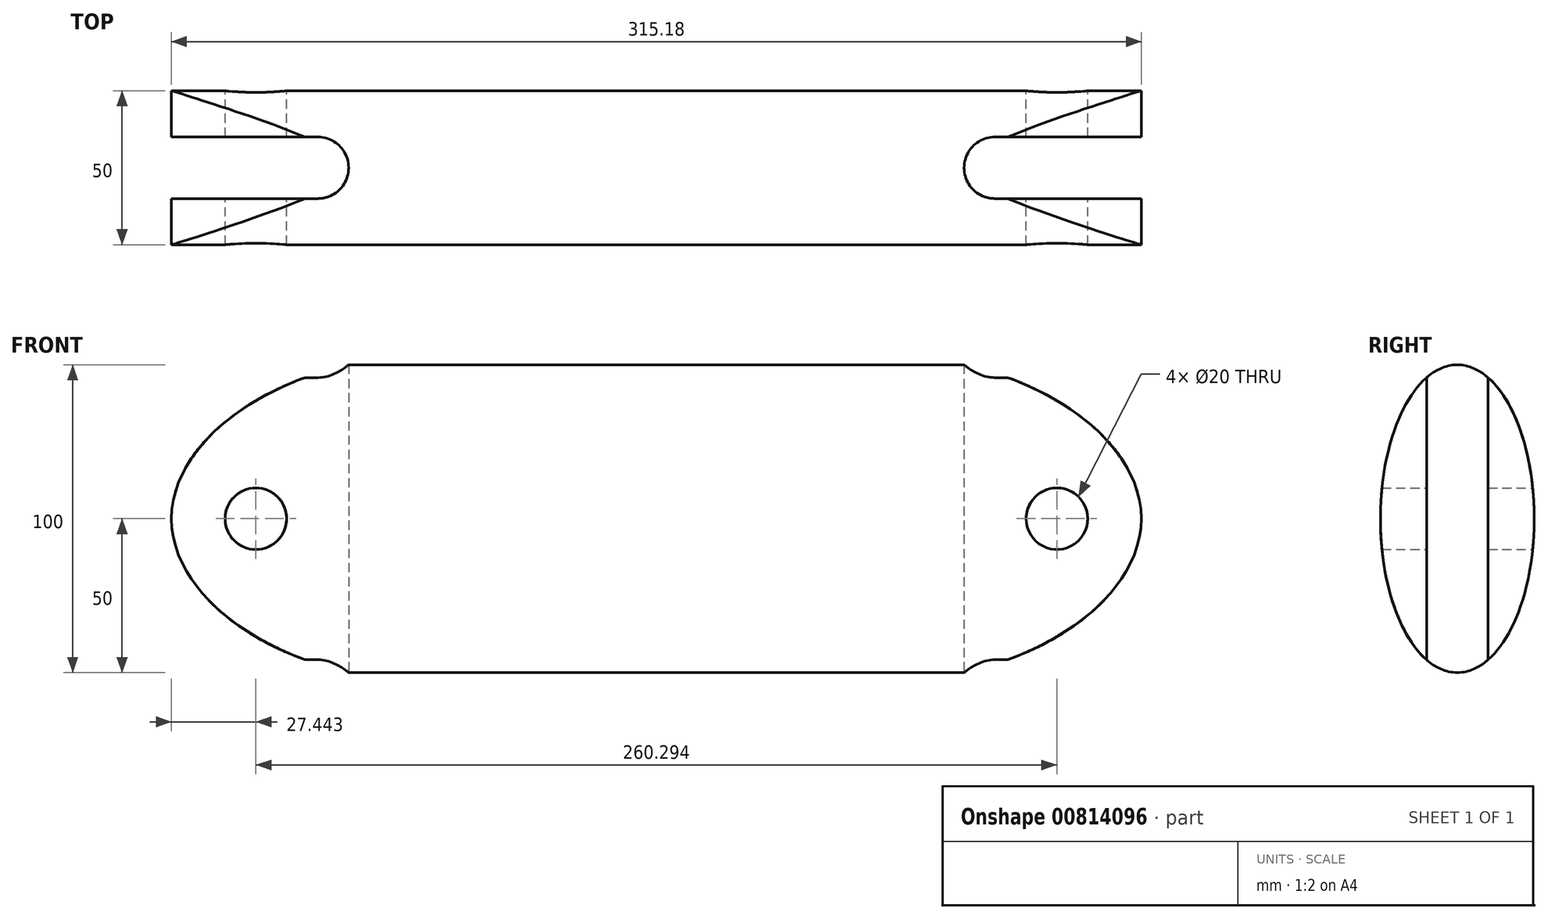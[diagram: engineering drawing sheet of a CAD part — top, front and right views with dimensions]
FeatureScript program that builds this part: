
annotation { "Feature Type Name" : "Feature", "Feature Type Description" : "" }
export const myFeature = defineFeature(function(context is Context, id is Id, definition is map)
    precondition{}
    {
        {
            var Q0;
            Q0=qCreatedBy(makeId("Right.planeOp"),FACE);
            var sketch = newSketch(context, id + "F0", { "sketchPlane" : qUnion([Q0])});
            skEllipse(sketch, "E0", {"center": v(0, 0) * mm, "majorRadius": 50 * mm, "minorRadius": 25 * mm, "majorAxis": v(0, 1)});
            skSolve(sketch);
        }
        {
            var Q0;
            Q0=makeQuery(id+"F0.imprint","IMPRINT",FACE,{"disambiguationData":[TD([[makeQuery(id+"F0.imprint","IMPRINT",EDGE,{"derivedFrom":sQuery(id+"F0.wireOp",EDGE,"E0")}),1.0]])]});
            extrude(context, id + "F1", {"entities" : qUnion([Q0]), "depth" : 100 * mm, "offsetDistance" : 25 * mm});
        }
        {
            var Q0;
            Q0=qCreatedBy(makeId("Front.planeOp"),FACE);
            var sketch = newSketch(context, id + "F2", { "sketchPlane" : qUnion([Q0])});
            skLineSegment(sketch, "E1", {"start": v(100, 50) * mm, "end": v(100, -50) * mm});
            skFitSpline(sketch, "E2", {"points": [v(100, 50) * mm, v(157.59, 0) * mm, v(100, -50) * mm], "startDerivative": vector(210, -48) * mm, "endDerivative": vector(-210, -48) * mm});
            skCircle(sketch, "E3", {"center": v(130.15, 0) * mm, "radius": 10 * mm});
            skSolve(sketch);
        }
        {
            var Q0;
            Q0=makeQuery(id+"F2.imprint","IMPRINT",FACE,{"disambiguationData":[TD([[makeQuery(id+"F2.imprint","IMPRINT",EDGE,{"derivedFrom":sQuery(id+"F2.wireOp",EDGE,"E1")}),1.0]])]});
            extrude(context, id + "F3", {"entities" : qUnion([Q0]), "operationType" : NewBodyOperationType.ADD, "endBound" : BoundingType.SYMMETRIC, "depth" : 50 * mm, "offsetDistance" : 25 * mm});
        }
        {
            var Q0;
            Q0 = qSketchRegion(id + "F2", true);
            extrude(context, id + "F4", {"entities" : qUnion([Q0]), "operationType" : NewBodyOperationType.REMOVE, "endBound" : BoundingType.SYMMETRIC, "depth" : 20 * mm, "offsetDistance" : 25 * mm});
        }
        {
            var Q0;
            {var subQ0=sQuery(id+"F2.wireOp",EDGE,"E2");var subQ1=sQuery(id+"F2.wireOp",EDGE,"E1");var subQ2=makeQuery(id+"F3.opExtrude","SWEPT_FACE",FACE,{"disambiguationData":[OSD([subQ1])]});Q0=makeQuery(id+"F3.boolean.opBoolean","SPLIT",FACE,{"disambiguationData":[TD([makeQuery(id+"F1.opExtrude","SWEPT_FACE",FACE,{"disambiguationData":[OSD([sQuery(id+"F0.wireOp",EDGE,"E0")])]}),subQ2,makeQuery(id+"F3.opExtrude","CAP_FACE",FACE,{"disambiguationData":[OSD([subQ1,subQ0,sQuery(id+"F2.wireOp",EDGE,"E3")])],"isStart":false}),makeQuery(id+"F3.opExtrude","SWEPT_FACE",FACE,{"disambiguationData":[OSD([subQ0])]})]),OD(0.0)],"derivedFrom":subQ2});}
            var Q1;
            {var subQ0=sQuery(id+"F2.wireOp",EDGE,"E1");var subQ1=makeQuery(id+"F3.opExtrude","SWEPT_FACE",FACE,{"disambiguationData":[OSD([subQ0])]});var subQ2=sQuery(id+"F2.wireOp",EDGE,"E2");Q1=makeQuery(id+"F3.boolean.opBoolean","SPLIT",FACE,{"disambiguationData":[TD([makeQuery(id+"F1.opExtrude","SWEPT_FACE",FACE,{"disambiguationData":[OSD([sQuery(id+"F0.wireOp",EDGE,"E0")])]}),subQ1,makeQuery(id+"F3.opExtrude","CAP_FACE",FACE,{"disambiguationData":[OSD([subQ0,subQ2,sQuery(id+"F2.wireOp",EDGE,"E3")])],"isStart":true}),makeQuery(id+"F3.opExtrude","SWEPT_FACE",FACE,{"disambiguationData":[OSD([subQ2])]})]),OD(0.0)],"derivedFrom":subQ1});}
            var Q2;
            {var subQ0=sQuery(id+"F2.wireOp",EDGE,"E2");var subQ1=sQuery(id+"F2.wireOp",EDGE,"E1");var subQ2=makeQuery(id+"F3.opExtrude","SWEPT_FACE",FACE,{"disambiguationData":[OSD([subQ1])]});Q2=makeQuery(id+"F3.boolean.opBoolean","SPLIT",FACE,{"disambiguationData":[TD([makeQuery(id+"F1.opExtrude","SWEPT_FACE",FACE,{"disambiguationData":[OSD([sQuery(id+"F0.wireOp",EDGE,"E0")])]}),subQ2,makeQuery(id+"F3.opExtrude","CAP_FACE",FACE,{"disambiguationData":[OSD([subQ1,subQ0,sQuery(id+"F2.wireOp",EDGE,"E3")])],"isStart":false}),makeQuery(id+"F3.opExtrude","SWEPT_FACE",FACE,{"disambiguationData":[OSD([subQ0])]})]),OD(1.0)],"derivedFrom":subQ2});}
            var Q3;
            {var subQ0=sQuery(id+"F2.wireOp",EDGE,"E1");var subQ1=makeQuery(id+"F3.opExtrude","SWEPT_FACE",FACE,{"disambiguationData":[OSD([subQ0])]});var subQ2=sQuery(id+"F2.wireOp",EDGE,"E2");Q3=makeQuery(id+"F3.boolean.opBoolean","SPLIT",FACE,{"disambiguationData":[TD([makeQuery(id+"F1.opExtrude","SWEPT_FACE",FACE,{"disambiguationData":[OSD([sQuery(id+"F0.wireOp",EDGE,"E0")])]}),subQ1,makeQuery(id+"F3.opExtrude","CAP_FACE",FACE,{"disambiguationData":[OSD([subQ0,subQ2,sQuery(id+"F2.wireOp",EDGE,"E3")])],"isStart":true}),makeQuery(id+"F3.opExtrude","SWEPT_FACE",FACE,{"disambiguationData":[OSD([subQ2])]})]),OD(1.0)],"derivedFrom":subQ1});}
            extrude(context, id + "F5", {"entities" : qUnion([Q0, Q1, Q2, Q3]), "operationType" : NewBodyOperationType.REMOVE, "oppositeDirection" : true, "depth" : 66 * mm, "offsetDistance" : 25 * mm});
        }
        {
            var Q0;
            {var subQ0=sQuery(id+"F2.wireOp",EDGE,"E1");Q0=makeQuery(id+"F4.boolean.opBoolean","COPY",EDGE,{"disambiguationData":[topologyDisambiguationEdgeConnected([makeQuery(id+"F4.opExtrude","SWEPT_FACE",FACE,{"disambiguationData":[OSD([subQ0])]}),makeQuery(id+"F4.opExtrude","CAP_FACE",FACE,{"disambiguationData":[OSD([subQ0,sQuery(id+"F2.wireOp",EDGE,"E2"),sQuery(id+"F2.wireOp",EDGE,"E3")])],"isStart":false})])],"derivedFrom":makeQuery(id+"F4.opExtrude","CAP_EDGE",EDGE,{"disambiguationData":[OSD([subQ0])],"isStart":false})});}
            var Q1;
            {var subQ0=sQuery(id+"F2.wireOp",EDGE,"E1");Q1=makeQuery(id+"F4.boolean.opBoolean","COPY",EDGE,{"disambiguationData":[topologyDisambiguationEdgeConnected([makeQuery(id+"F4.opExtrude","SWEPT_FACE",FACE,{"disambiguationData":[OSD([subQ0])]}),makeQuery(id+"F4.opExtrude","CAP_FACE",FACE,{"disambiguationData":[OSD([subQ0,sQuery(id+"F2.wireOp",EDGE,"E2"),sQuery(id+"F2.wireOp",EDGE,"E3")])],"isStart":true})])],"derivedFrom":makeQuery(id+"F4.opExtrude","CAP_EDGE",EDGE,{"disambiguationData":[OSD([subQ0])],"isStart":true})});}
            fillet(context, id + "F6", {"entities" : qUnion([Q0, Q1]), "radius" : 10 * mm, "tangentPropagation" : true, "allowEdgeOverflow" : false});
        }
        {
            var Q0;
            Q0=makeQuery(id+"F1.opExtrude","SWEPT_BODY",BODY,{"disambiguationData":[OSD([sQuery(id+"F0.wireOp",EDGE,"E0")])]});
            var Q1;
            Q1=qCreatedBy(makeId("Right.planeOp"),FACE);
            mirror(context, id + "F7", {"operationType" : NewBodyOperationType.ADD, "entities" : qUnion([Q0]), "mirrorPlane" : qUnion([Q1])});
        }
    });
